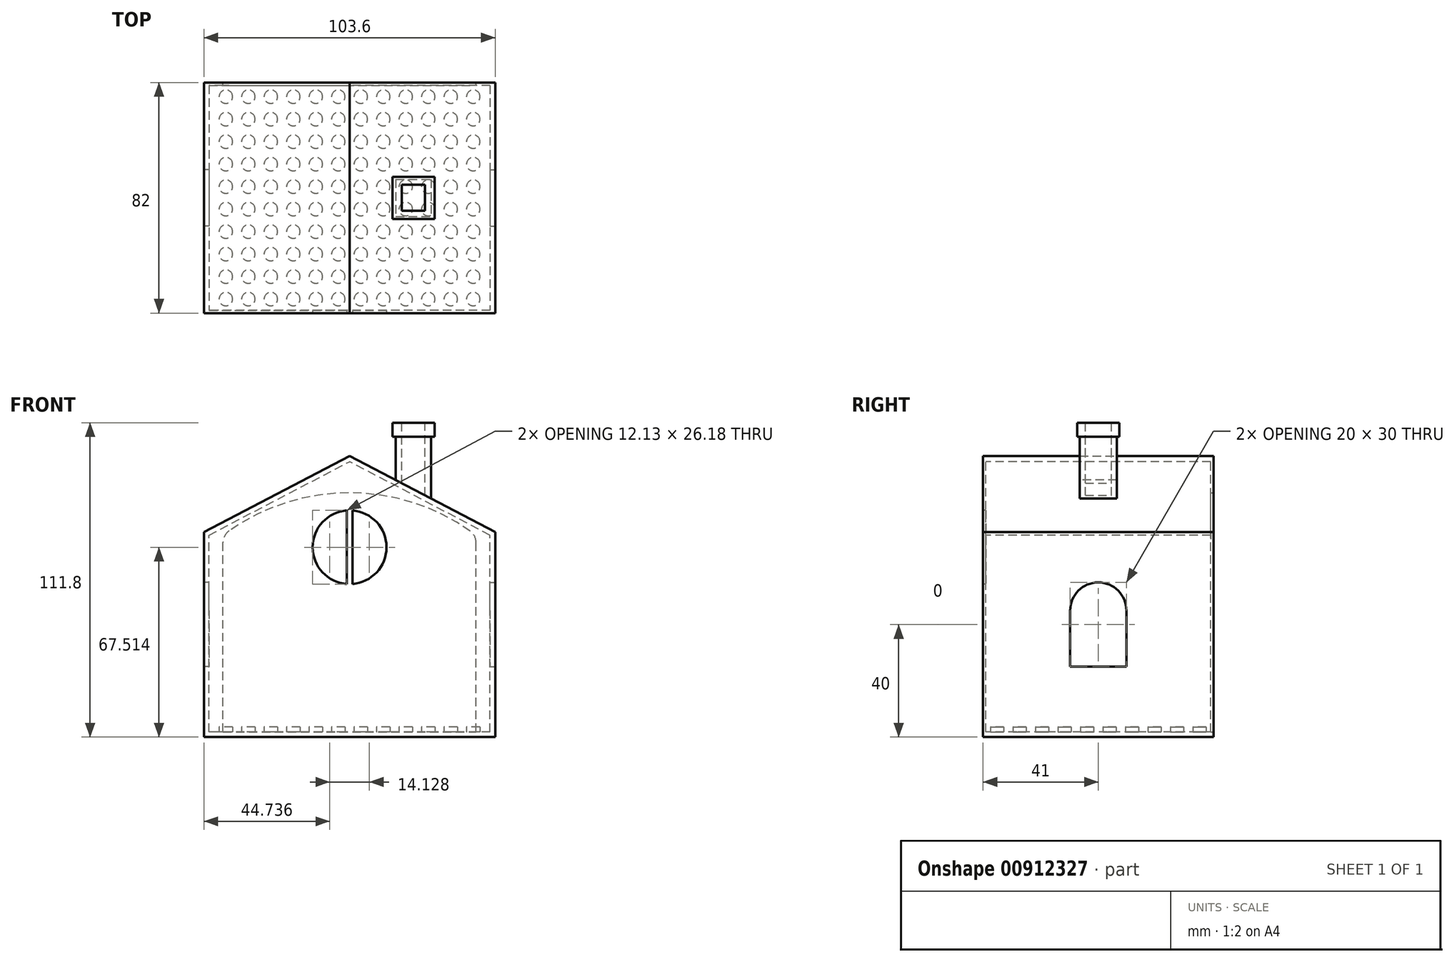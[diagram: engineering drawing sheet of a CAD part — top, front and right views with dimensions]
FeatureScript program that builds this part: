
annotation { "Feature Type Name" : "Feature", "Feature Type Description" : "" }
export const myFeature = defineFeature(function(context is Context, id is Id, definition is map)
    precondition{}
    {
        {
            var Q0;
            Q0=qCreatedBy(makeId("Front.planeOp"),FACE);
            var sketch = newSketch(context, id + "F0", { "sketchPlane" : qUnion([Q0])});
            skLineSegment(sketch, "E0", {"start": v(0, 0) * mm, "end": v(50, 0) * mm});
            skLineSegment(sketch, "E1", {"start": v(50, 0) * mm, "end": v(50, 70) * mm});
            skLineSegment(sketch, "E2", {"start": v(50, 70) * mm, "end": v(0, 96.17) * mm});
            skLineSegment(sketch, "E3", {"start": v(0, 96.17) * mm, "end": v(0, 0) * mm, "construction": true});
            skLineSegment(sketch, "E4.MirrorCS", {"start": v(-50, 70) * mm, "end": v(0, 96.17) * mm});
            skLineSegment(sketch, "E5.MirrorCS", {"start": v(-50, 0) * mm, "end": v(-50, 70) * mm});
            skLineSegment(sketch, "E6.MirrorCS", {"start": v(0, 0) * mm, "end": v(-50, 0) * mm});
            skLineSegment(sketch, "E7.0", {"start": v(0, -1.8) * mm, "end": v(51.8, -1.8) * mm});
            skLineSegment(sketch, "E7.1", {"start": v(51.8, 71.09) * mm, "end": v(0, 98.2) * mm});
            skLineSegment(sketch, "E7.2", {"start": v(-51.8, 71.09) * mm, "end": v(0, 98.2) * mm});
            skLineSegment(sketch, "E7.3", {"start": v(51.8, -1.8) * mm, "end": v(51.8, 71.09) * mm});
            skLineSegment(sketch, "E7.4", {"start": v(-51.8, -1.8) * mm, "end": v(-51.8, 71.09) * mm});
            skLineSegment(sketch, "E7.5", {"start": v(0, -1.8) * mm, "end": v(-51.8, -1.8) * mm});
            skSolve(sketch);
        }
        {
            var Q0;
            Q0=makeQuery(id+"F0.imprint","IMPRINT",FACE,{"disambiguationData":[TD([[makeQuery(id+"F0.imprint","IMPRINT",EDGE,{"derivedFrom":sQuery(id+"F0.wireOp",EDGE,"E0")}),-1.0]])]});
            var Q1;
            Q1=makeQuery(id+"F0.imprint","IMPRINT",FACE,{"disambiguationData":[TD([[makeQuery(id+"F0.imprint","IMPRINT",EDGE,{"derivedFrom":sQuery(id+"F0.wireOp",EDGE,"E0")}),1.0]])]});
            extrude(context, id + "F1", {"entities" : qUnion([Q0, Q1]), "endBound" : BoundingType.SYMMETRIC, "depth" : 82 * mm, "offsetDistance" : 25 * mm});
        }
        {
            var Q0;
            Q0=makeQuery(id+"F1.opExtrude","SWEPT_FACE",FACE,{"disambiguationData":[OSD([sQuery(id+"F0.wireOp",EDGE,"E7.4")])]});
            var sketch = newSketch(context, id + "F2", { "sketchPlane" : qUnion([Q0])});
            skLineSegment(sketch, "E8.top", {"start": v(-10, 23.2) * mm, "end": v(10, 23.2) * mm});
            skLineSegment(sketch, "E8.left", {"start": v(-10, 43.2) * mm, "end": v(-10, 23.2) * mm});
            skLineSegment(sketch, "E8.right", {"start": v(10, 43.2) * mm, "end": v(10, 23.2) * mm});
            skArc(sketch, "E9", {"start": v(10, 43.2) * mm, "mid": v(0, 53.2) * mm, "end": v(-10, 43.2) * mm});
            skSolve(sketch);
        }
        {
            var Q0;
            Q0=makeQuery(id+"F2.imprint","IMPRINT",FACE,{"disambiguationData":[TD([[makeQuery(id+"F2.imprint","IMPRINT",EDGE,{"derivedFrom":sQuery(id+"F2.wireOp",EDGE,"E8.bottom")}),-1.0]])]});
            var Q1;
            Q1=makeQuery(id+"F2.imprint","IMPRINT",FACE,{"disambiguationData":[TD([[makeQuery(id+"F2.imprint","IMPRINT",EDGE,{"derivedFrom":sQuery(id+"F2.wireOp",EDGE,"E8.top")}),1.0]])]});
            extrude(context, id + "F3", {"entities" : qUnion([Q0, Q1]), "operationType" : NewBodyOperationType.REMOVE, "oppositeDirection" : true, "depth" : 25 * mm, "offsetDistance" : 25 * mm});
        }
        {
            var Q0;
            Q0=makeQuery(id+"F1.opExtrude","SWEPT_FACE",FACE,{"disambiguationData":[OSD([sQuery(id+"F0.wireOp",EDGE,"E7.3")])]});
            var sketch = newSketch(context, id + "F4", { "sketchPlane" : qUnion([Q0])});
            skLineSegment(sketch, "E10.top", {"start": v(-10, 23.2) * mm, "end": v(10, 23.2) * mm});
            skLineSegment(sketch, "E10.left", {"start": v(-10, 43.2) * mm, "end": v(-10, 23.2) * mm});
            skLineSegment(sketch, "E10.right", {"start": v(10, 43.2) * mm, "end": v(10, 23.2) * mm});
            skArc(sketch, "E11", {"start": v(10, 43.2) * mm, "mid": v(0, 53.2) * mm, "end": v(-10, 43.2) * mm});
            skSolve(sketch);
        }
        {
            var Q0;
            Q0=makeQuery(id+"F4.imprint","IMPRINT",FACE,{"disambiguationData":[TD([[makeQuery(id+"F4.imprint","IMPRINT",EDGE,{"derivedFrom":sQuery(id+"F4.wireOp",EDGE,"E10.top")}),1.0]])]});
            extrude(context, id + "F5", {"entities" : qUnion([Q0]), "operationType" : NewBodyOperationType.REMOVE, "oppositeDirection" : true, "depth" : 25 * mm, "offsetDistance" : 25 * mm});
        }
        {
            var Q0;
            Q0=qCreatedBy(makeId("Front.planeOp"),FACE);
            cPlane(context, id + "F6", {"entities" : qUnion([Q0]), "cplaneType" : CPlaneType.OFFSET, "offset" : 40 * mm, "width" : 150 * mm, "height" : 150 * mm});
        }
        {
            var Q0;
            Q0=makeQuery(id+"F0.imprint","IMPRINT",FACE,{"disambiguationData":[TD([[makeQuery(id+"F0.imprint","IMPRINT",EDGE,{"derivedFrom":sQuery(id+"F0.wireOp",EDGE,"E0")}),1.0]])]});
            extrude(context, id + "F7", {"entities" : qUnion([Q0]), "operationType" : NewBodyOperationType.REMOVE, "oppositeDirection" : true, "depth" : 40 * mm, "offsetDistance" : 25 * mm});
        }
        {
            var Q0;
            Q0=makeQuery(id+"F0.imprint","IMPRINT",FACE,{"disambiguationData":[TD([[makeQuery(id+"F0.imprint","IMPRINT",EDGE,{"derivedFrom":sQuery(id+"F0.wireOp",EDGE,"E0")}),1.0]])]});
            extrude(context, id + "F8", {"entities" : qUnion([Q0]), "operationType" : NewBodyOperationType.REMOVE, "depth" : 40 * mm, "offsetDistance" : 25 * mm});
        }
        {
            var Q0;
            Q0=makeQuery(id+"F1.opExtrude","CAP_FACE",FACE,{"disambiguationData":[OSD([sQuery(id+"F0.wireOp",EDGE,"E7.0"),sQuery(id+"F0.wireOp",EDGE,"E7.1"),sQuery(id+"F0.wireOp",EDGE,"E7.2"),sQuery(id+"F0.wireOp",EDGE,"E7.3"),sQuery(id+"F0.wireOp",EDGE,"E7.4"),sQuery(id+"F0.wireOp",EDGE,"E7.5")])],"isStart":false});
            var sketch = newSketch(context, id + "F9", { "sketchPlane" : qUnion([Q0])});
            skCircle(sketch, "E12", {"center": v(0, 65.71) * mm, "radius": 13.13 * mm});
            skLineSegment(sketch, "E13", {"start": v(-13.13, 65.96) * mm, "end": v(13.13, 65.96) * mm, "construction": true});
            skLineSegment(sketch, "E14", {"start": v(0, 78.84) * mm, "end": v(0, 52.59) * mm, "construction": true});
            skLineSegment(sketch, "E15.0", {"start": v(-1, 78.84) * mm, "end": v(-1, 52.59) * mm});
            skLineSegment(sketch, "E16.0", {"start": v(1, 78.84) * mm, "end": v(1, 52.59) * mm});
            skSolve(sketch);
        }
        {
            var Q0;
            Q0=qCreatedBy(makeId("Top.planeOp"),FACE);
            var sketch = newSketch(context, id + "F10", { "sketchPlane" : qUnion([Q0])});
            skCircle(sketch, "E17", {"center": v(-44, 36) * mm, "radius": 2.4 * mm});
            skCircle(sketch, "E18.0.1.0", {"center": v(-44, 28) * mm, "radius": 2.4 * mm});
            skCircle(sketch, "E18.0.2.0", {"center": v(-44, 20) * mm, "radius": 2.4 * mm});
            skCircle(sketch, "E18.0.3.0", {"center": v(-44, 12) * mm, "radius": 2.4 * mm});
            skCircle(sketch, "E18.0.4.0", {"center": v(-44, 4) * mm, "radius": 2.4 * mm});
            skCircle(sketch, "E18.0.5.0", {"center": v(-44, -4) * mm, "radius": 2.4 * mm});
            skCircle(sketch, "E18.0.6.0", {"center": v(-44, -12) * mm, "radius": 2.4 * mm});
            skCircle(sketch, "E18.0.7.0", {"center": v(-44, -20) * mm, "radius": 2.4 * mm});
            skCircle(sketch, "E18.0.8.0", {"center": v(-44, -28) * mm, "radius": 2.4 * mm});
            skCircle(sketch, "E18.0.9.0", {"center": v(-44, -36) * mm, "radius": 2.4 * mm});
            skCircle(sketch, "E18.1.0.0", {"center": v(-36, 36) * mm, "radius": 2.4 * mm});
            skCircle(sketch, "E18.1.1.0", {"center": v(-36, 28) * mm, "radius": 2.4 * mm});
            skCircle(sketch, "E18.1.2.0", {"center": v(-36, 20) * mm, "radius": 2.4 * mm});
            skCircle(sketch, "E18.1.3.0", {"center": v(-36, 12) * mm, "radius": 2.4 * mm});
            skCircle(sketch, "E18.1.4.0", {"center": v(-36, 4) * mm, "radius": 2.4 * mm});
            skCircle(sketch, "E18.1.5.0", {"center": v(-36, -4) * mm, "radius": 2.4 * mm});
            skCircle(sketch, "E18.1.6.0", {"center": v(-36, -12) * mm, "radius": 2.4 * mm});
            skCircle(sketch, "E18.1.7.0", {"center": v(-36, -20) * mm, "radius": 2.4 * mm});
            skCircle(sketch, "E18.1.8.0", {"center": v(-36, -28) * mm, "radius": 2.4 * mm});
            skCircle(sketch, "E18.1.9.0", {"center": v(-36, -36) * mm, "radius": 2.4 * mm});
            skCircle(sketch, "E18.2.0.0", {"center": v(-28, 36) * mm, "radius": 2.4 * mm});
            skCircle(sketch, "E18.2.1.0", {"center": v(-28, 28) * mm, "radius": 2.4 * mm});
            skCircle(sketch, "E18.2.2.0", {"center": v(-28, 20) * mm, "radius": 2.4 * mm});
            skCircle(sketch, "E18.2.3.0", {"center": v(-28, 12) * mm, "radius": 2.4 * mm});
            skCircle(sketch, "E18.2.4.0", {"center": v(-28, 4) * mm, "radius": 2.4 * mm});
            skCircle(sketch, "E18.2.5.0", {"center": v(-28, -4) * mm, "radius": 2.4 * mm});
            skCircle(sketch, "E18.2.6.0", {"center": v(-28, -12) * mm, "radius": 2.4 * mm});
            skCircle(sketch, "E18.2.7.0", {"center": v(-28, -20) * mm, "radius": 2.4 * mm});
            skCircle(sketch, "E18.2.8.0", {"center": v(-28, -28) * mm, "radius": 2.4 * mm});
            skCircle(sketch, "E18.2.9.0", {"center": v(-28, -36) * mm, "radius": 2.4 * mm});
            skCircle(sketch, "E18.3.0.0", {"center": v(-20, 36) * mm, "radius": 2.4 * mm});
            skCircle(sketch, "E18.3.1.0", {"center": v(-20, 28) * mm, "radius": 2.4 * mm});
            skCircle(sketch, "E18.3.2.0", {"center": v(-20, 20) * mm, "radius": 2.4 * mm});
            skCircle(sketch, "E18.3.3.0", {"center": v(-20, 12) * mm, "radius": 2.4 * mm});
            skCircle(sketch, "E18.3.4.0", {"center": v(-20, 4) * mm, "radius": 2.4 * mm});
            skCircle(sketch, "E18.3.5.0", {"center": v(-20, -4) * mm, "radius": 2.4 * mm});
            skCircle(sketch, "E18.3.6.0", {"center": v(-20, -12) * mm, "radius": 2.4 * mm});
            skCircle(sketch, "E18.3.7.0", {"center": v(-20, -20) * mm, "radius": 2.4 * mm});
            skCircle(sketch, "E18.3.8.0", {"center": v(-20, -28) * mm, "radius": 2.4 * mm});
            skCircle(sketch, "E18.3.9.0", {"center": v(-20, -36) * mm, "radius": 2.4 * mm});
            skCircle(sketch, "E18.4.0.0", {"center": v(-12, 36) * mm, "radius": 2.4 * mm});
            skCircle(sketch, "E18.4.1.0", {"center": v(-12, 28) * mm, "radius": 2.4 * mm});
            skCircle(sketch, "E18.4.2.0", {"center": v(-12, 20) * mm, "radius": 2.4 * mm});
            skCircle(sketch, "E18.4.3.0", {"center": v(-12, 12) * mm, "radius": 2.4 * mm});
            skCircle(sketch, "E18.4.4.0", {"center": v(-12, 4) * mm, "radius": 2.4 * mm});
            skCircle(sketch, "E18.4.5.0", {"center": v(-12, -4) * mm, "radius": 2.4 * mm});
            skCircle(sketch, "E18.4.6.0", {"center": v(-12, -12) * mm, "radius": 2.4 * mm});
            skCircle(sketch, "E18.4.7.0", {"center": v(-12, -20) * mm, "radius": 2.4 * mm});
            skCircle(sketch, "E18.4.8.0", {"center": v(-12, -28) * mm, "radius": 2.4 * mm});
            skCircle(sketch, "E18.4.9.0", {"center": v(-12, -36) * mm, "radius": 2.4 * mm});
            skCircle(sketch, "E18.5.0.0", {"center": v(-4, 36) * mm, "radius": 2.4 * mm});
            skCircle(sketch, "E18.5.1.0", {"center": v(-4, 28) * mm, "radius": 2.4 * mm});
            skCircle(sketch, "E18.5.2.0", {"center": v(-4, 20) * mm, "radius": 2.4 * mm});
            skCircle(sketch, "E18.5.3.0", {"center": v(-4, 12) * mm, "radius": 2.4 * mm});
            skCircle(sketch, "E18.5.4.0", {"center": v(-4, 4) * mm, "radius": 2.4 * mm});
            skCircle(sketch, "E18.5.5.0", {"center": v(-4, -4) * mm, "radius": 2.4 * mm});
            skCircle(sketch, "E18.5.6.0", {"center": v(-4, -12) * mm, "radius": 2.4 * mm});
            skCircle(sketch, "E18.5.7.0", {"center": v(-4, -20) * mm, "radius": 2.4 * mm});
            skCircle(sketch, "E18.5.8.0", {"center": v(-4, -28) * mm, "radius": 2.4 * mm});
            skCircle(sketch, "E18.5.9.0", {"center": v(-4, -36) * mm, "radius": 2.4 * mm});
            skCircle(sketch, "E18.6.0.0", {"center": v(4, 36) * mm, "radius": 2.4 * mm});
            skCircle(sketch, "E18.6.1.0", {"center": v(4, 28) * mm, "radius": 2.4 * mm});
            skCircle(sketch, "E18.6.2.0", {"center": v(4, 20) * mm, "radius": 2.4 * mm});
            skCircle(sketch, "E18.6.3.0", {"center": v(4, 12) * mm, "radius": 2.4 * mm});
            skCircle(sketch, "E18.6.4.0", {"center": v(4, 4) * mm, "radius": 2.4 * mm});
            skCircle(sketch, "E18.6.5.0", {"center": v(4, -4) * mm, "radius": 2.4 * mm});
            skCircle(sketch, "E18.6.6.0", {"center": v(4, -12) * mm, "radius": 2.4 * mm});
            skCircle(sketch, "E18.6.7.0", {"center": v(4, -20) * mm, "radius": 2.4 * mm});
            skCircle(sketch, "E18.6.8.0", {"center": v(4, -28) * mm, "radius": 2.4 * mm});
            skCircle(sketch, "E18.6.9.0", {"center": v(4, -36) * mm, "radius": 2.4 * mm});
            skCircle(sketch, "E18.7.0.0", {"center": v(12, 36) * mm, "radius": 2.4 * mm});
            skCircle(sketch, "E18.7.1.0", {"center": v(12, 28) * mm, "radius": 2.4 * mm});
            skCircle(sketch, "E18.7.2.0", {"center": v(12, 20) * mm, "radius": 2.4 * mm});
            skCircle(sketch, "E18.7.3.0", {"center": v(12, 12) * mm, "radius": 2.4 * mm});
            skCircle(sketch, "E18.7.4.0", {"center": v(12, 4) * mm, "radius": 2.4 * mm});
            skCircle(sketch, "E18.7.5.0", {"center": v(12, -4) * mm, "radius": 2.4 * mm});
            skCircle(sketch, "E18.7.6.0", {"center": v(12, -12) * mm, "radius": 2.4 * mm});
            skCircle(sketch, "E18.7.7.0", {"center": v(12, -20) * mm, "radius": 2.4 * mm});
            skCircle(sketch, "E18.7.8.0", {"center": v(12, -28) * mm, "radius": 2.4 * mm});
            skCircle(sketch, "E18.7.9.0", {"center": v(12, -36) * mm, "radius": 2.4 * mm});
            skCircle(sketch, "E18.8.0.0", {"center": v(20, 36) * mm, "radius": 2.4 * mm});
            skCircle(sketch, "E18.8.1.0", {"center": v(20, 28) * mm, "radius": 2.4 * mm});
            skCircle(sketch, "E18.8.2.0", {"center": v(20, 20) * mm, "radius": 2.4 * mm});
            skCircle(sketch, "E18.8.3.0", {"center": v(20, 12) * mm, "radius": 2.4 * mm});
            skCircle(sketch, "E18.8.4.0", {"center": v(20, 4) * mm, "radius": 2.4 * mm});
            skCircle(sketch, "E18.8.5.0", {"center": v(20, -4) * mm, "radius": 2.4 * mm});
            skCircle(sketch, "E18.8.6.0", {"center": v(20, -12) * mm, "radius": 2.4 * mm});
            skCircle(sketch, "E18.8.7.0", {"center": v(20, -20) * mm, "radius": 2.4 * mm});
            skCircle(sketch, "E18.8.8.0", {"center": v(20, -28) * mm, "radius": 2.4 * mm});
            skCircle(sketch, "E18.8.9.0", {"center": v(20, -36) * mm, "radius": 2.4 * mm});
            skCircle(sketch, "E18.9.0.0", {"center": v(28, 36) * mm, "radius": 2.4 * mm});
            skCircle(sketch, "E18.9.1.0", {"center": v(28, 28) * mm, "radius": 2.4 * mm});
            skCircle(sketch, "E18.9.2.0", {"center": v(28, 20) * mm, "radius": 2.4 * mm});
            skCircle(sketch, "E18.9.3.0", {"center": v(28, 12) * mm, "radius": 2.4 * mm});
            skCircle(sketch, "E18.9.4.0", {"center": v(28, 4) * mm, "radius": 2.4 * mm});
            skCircle(sketch, "E18.9.5.0", {"center": v(28, -4) * mm, "radius": 2.4 * mm});
            skCircle(sketch, "E18.9.6.0", {"center": v(28, -12) * mm, "radius": 2.4 * mm});
            skCircle(sketch, "E18.9.7.0", {"center": v(28, -20) * mm, "radius": 2.4 * mm});
            skCircle(sketch, "E18.9.8.0", {"center": v(28, -28) * mm, "radius": 2.4 * mm});
            skCircle(sketch, "E18.9.9.0", {"center": v(28, -36) * mm, "radius": 2.4 * mm});
            skCircle(sketch, "E18.10.0.0", {"center": v(36, 36) * mm, "radius": 2.4 * mm});
            skCircle(sketch, "E18.10.1.0", {"center": v(36, 28) * mm, "radius": 2.4 * mm});
            skCircle(sketch, "E18.10.2.0", {"center": v(36, 20) * mm, "radius": 2.4 * mm});
            skCircle(sketch, "E18.10.3.0", {"center": v(36, 12) * mm, "radius": 2.4 * mm});
            skCircle(sketch, "E18.10.4.0", {"center": v(36, 4) * mm, "radius": 2.4 * mm});
            skCircle(sketch, "E18.10.5.0", {"center": v(36, -4) * mm, "radius": 2.4 * mm});
            skCircle(sketch, "E18.10.6.0", {"center": v(36, -12) * mm, "radius": 2.4 * mm});
            skCircle(sketch, "E18.10.7.0", {"center": v(36, -20) * mm, "radius": 2.4 * mm});
            skCircle(sketch, "E18.10.8.0", {"center": v(36, -28) * mm, "radius": 2.4 * mm});
            skCircle(sketch, "E18.10.9.0", {"center": v(36, -36) * mm, "radius": 2.4 * mm});
            skCircle(sketch, "E18.11.0.0", {"center": v(44, 36) * mm, "radius": 2.4 * mm});
            skCircle(sketch, "E18.11.1.0", {"center": v(44, 28) * mm, "radius": 2.4 * mm});
            skCircle(sketch, "E18.11.2.0", {"center": v(44, 20) * mm, "radius": 2.4 * mm});
            skCircle(sketch, "E18.11.3.0", {"center": v(44, 12) * mm, "radius": 2.4 * mm});
            skCircle(sketch, "E18.11.4.0", {"center": v(44, 4) * mm, "radius": 2.4 * mm});
            skCircle(sketch, "E18.11.5.0", {"center": v(44, -4) * mm, "radius": 2.4 * mm});
            skCircle(sketch, "E18.11.6.0", {"center": v(44, -12) * mm, "radius": 2.4 * mm});
            skCircle(sketch, "E18.11.7.0", {"center": v(44, -20) * mm, "radius": 2.4 * mm});
            skCircle(sketch, "E18.11.8.0", {"center": v(44, -28) * mm, "radius": 2.4 * mm});
            skCircle(sketch, "E18.11.9.0", {"center": v(44, -36) * mm, "radius": 2.4 * mm});
            skLineSegment(sketch, "E18.direction1", {"start": v(-44, 36) * mm, "end": v(-36, 36) * mm, "construction": true});
            skLineSegment(sketch, "E18.direction2", {"start": v(-44, 36) * mm, "end": v(-44, 28) * mm, "construction": true});
            skSolve(sketch);
        }
        {
            var Q0;
            Q0=qSketchRegion(id+"F10",true);
            extrude(context, id + "F11", {"entities" : qUnion([Q0]), "operationType" : NewBodyOperationType.ADD, "depth" : 1.8 * mm, "offsetDistance" : 25 * mm});
        }
        {
            var Q0;
            {var subQ0=sQuery(id+"F9.wireOp",EDGE,"E15.0");var subQ1=sQuery(id+"F9.wireOp",EDGE,"E12");var subQ2=makeQuery(id+"F9.imprint","INTERSECT",VERTEX,{"disambiguationData":[OD(0.0)],"derivedFrom":[subQ1,subQ0]});Q0=makeQuery(id+"F9.imprint","IMPRINT",FACE,{"disambiguationData":[TD([[makeQuery(id+"F9.imprint","IMPRINT",EDGE,{"disambiguationData":[TD([[subQ2,-1.0]])],"derivedFrom":subQ1}),1.0]])]});}
            var Q1;
            {var subQ0=sQuery(id+"F9.wireOp",EDGE,"E16.0");var subQ1=sQuery(id+"F9.wireOp",EDGE,"E12");var subQ2=makeQuery(id+"F9.imprint","INTERSECT",VERTEX,{"disambiguationData":[OD(0.0)],"derivedFrom":[subQ1,subQ0]});Q1=makeQuery(id+"F9.imprint","IMPRINT",FACE,{"disambiguationData":[TD([[makeQuery(id+"F9.imprint","IMPRINT",EDGE,{"disambiguationData":[TD([[subQ2,1.0]])],"derivedFrom":subQ1}),1.0]])]});}
            extrude(context, id + "F12", {"entities" : qUnion([Q0, Q1]), "operationType" : NewBodyOperationType.REMOVE, "oppositeDirection" : true, "depth" : 25 * mm, "offsetDistance" : 25 * mm});
        }
        {
            var Q0;
            Q0=qCreatedBy(makeId("Top.planeOp"),FACE);
            cPlane(context, id + "F13", {"entities" : qUnion([Q0]), "cplaneType" : CPlaneType.OFFSET, "offset" : 110 * mm, "width" : 150 * mm, "height" : 150 * mm});
        }
        {
            var Q0;
            Q0=qCreatedBy(id+"F13.planeOp",FACE);
            var sketch = newSketch(context, id + "F14", { "sketchPlane" : qUnion([Q0])});
            skLineSegment(sketch, "E19.bottom", {"start": v(16.41, 6.6) * mm, "end": v(29.03, 6.6) * mm});
            skLineSegment(sketch, "E19.top", {"start": v(16.41, -6.6) * mm, "end": v(29.03, -6.6) * mm});
            skLineSegment(sketch, "E19.left", {"start": v(16.41, 6.6) * mm, "end": v(16.41, -6.6) * mm});
            skLineSegment(sketch, "E19.right", {"start": v(29.03, 6.6) * mm, "end": v(29.03, -6.6) * mm});
            skLineSegment(sketch, "E20", {"start": v(16.41, 0) * mm, "end": v(29.03, 0) * mm, "construction": true});
            skLineSegment(sketch, "E21", {"start": v(22.72, 6.6) * mm, "end": v(22.72, -6.6) * mm, "construction": true});
            skLineSegment(sketch, "E22.bottom", {"start": v(26.86, -4.63) * mm, "end": v(18.58, -4.63) * mm});
            skLineSegment(sketch, "E22.top", {"start": v(26.86, 4.63) * mm, "end": v(18.58, 4.63) * mm});
            skLineSegment(sketch, "E22.left", {"start": v(26.86, -4.63) * mm, "end": v(26.86, 4.63) * mm});
            skLineSegment(sketch, "E22.right", {"start": v(18.58, -4.63) * mm, "end": v(18.58, 4.63) * mm});
            skPoint(sketch, "E22.middle", {"position": v(22.72, 0) * mm});
            skLineSegment(sketch, "E23.bottom", {"start": v(30.22, -7.5) * mm, "end": v(15.21, -7.5) * mm});
            skLineSegment(sketch, "E23.top", {"start": v(30.22, 7.5) * mm, "end": v(15.21, 7.5) * mm});
            skLineSegment(sketch, "E23.left", {"start": v(30.22, -7.5) * mm, "end": v(30.22, 7.5) * mm});
            skLineSegment(sketch, "E23.right", {"start": v(15.21, -7.5) * mm, "end": v(15.21, 7.5) * mm});
            skSolve(sketch);
        }
        {
            var Q0;
            Q0=makeQuery(id+"F14.imprint","IMPRINT",FACE,{"disambiguationData":[TD([[makeQuery(id+"F14.imprint","IMPRINT",EDGE,{"derivedFrom":sQuery(id+"F14.wireOp",EDGE,"E19.bottom")}),-1.0]])]});
            extrude(context, id + "F15", {"entities" : qUnion([Q0]), "operationType" : NewBodyOperationType.ADD, "endBound" : BoundingType.UP_TO_NEXT, "oppositeDirection" : true, "depth" : 25 * mm, "offsetDistance" : 25 * mm});
        }
        {
            var Q0;
            Q0=makeQuery(id+"F14.imprint","IMPRINT",FACE,{"disambiguationData":[TD([[makeQuery(id+"F14.imprint","IMPRINT",EDGE,{"derivedFrom":sQuery(id+"F14.wireOp",EDGE,"E19.bottom")}),1.0]])]});
            extrude(context, id + "F16", {"entities" : qUnion([Q0]), "operationType" : NewBodyOperationType.ADD, "oppositeDirection" : true, "depth" : 5 * mm, "offsetDistance" : 25 * mm});
        }
        {
            var Q0;
            Q0=makeQuery(id+"F1.opExtrude","CAP_FACE",FACE,{"disambiguationData":[OSD([sQuery(id+"F0.wireOp",EDGE,"E7.0"),sQuery(id+"F0.wireOp",EDGE,"E7.1"),sQuery(id+"F0.wireOp",EDGE,"E7.2"),sQuery(id+"F0.wireOp",EDGE,"E7.3"),sQuery(id+"F0.wireOp",EDGE,"E7.4"),sQuery(id+"F0.wireOp",EDGE,"E7.5")])],"isStart":true});
            var sketch = newSketch(context, id + "F17", { "sketchPlane" : qUnion([Q0])});
            skLineSegment(sketch, "E24", {"start": v(45, 0) * mm, "end": v(-45, 0) * mm});
            skLineSegment(sketch, "E25", {"start": v(-45, 0) * mm, "end": v(-45, 70) * mm});
            skLineSegment(sketch, "E26", {"start": v(45, 0) * mm, "end": v(45, 70) * mm});
            skLineSegment(sketch, "E27", {"start": v(-45, 70) * mm, "end": v(45, 70) * mm, "construction": true});
            skArc(sketch, "E28", {"start": v(45, 70) * mm, "mid": v(0, 85.09) * mm, "end": v(-45, 70) * mm});
            skSolve(sketch);
        }
        {
            var Q0;
            Q0=makeQuery(id+"F17.imprint","IMPRINT",FACE,{"disambiguationData":[TD([[makeQuery(id+"F17.imprint","IMPRINT",EDGE,{"derivedFrom":sQuery(id+"F17.wireOp",EDGE,"E24")}),-1.0]])]});
            extrude(context, id + "F18", {"entities" : qUnion([Q0]), "operationType" : NewBodyOperationType.REMOVE, "oppositeDirection" : true, "depth" : 1 * mm, "offsetDistance" : 25 * mm});
        }
        {
            var Q0;
            Q0=makeQuery(id+"F18.boolean.opBoolean","COPY",EDGE,{"derivedFrom":makeQuery(id+"F18.opExtrude","SWEPT_EDGE",EDGE,{"disambiguationData":[OSD([sQuery(id+"F17.wireOp",EDGE,"E25"),sQuery(id+"F17.wireOp",EDGE,"E28")])]})});
            var Q1;
            Q1=makeQuery(id+"F18.boolean.opBoolean","COPY",EDGE,{"derivedFrom":makeQuery(id+"F18.opExtrude","SWEPT_EDGE",EDGE,{"disambiguationData":[OSD([sQuery(id+"F17.wireOp",EDGE,"E26"),sQuery(id+"F17.wireOp",EDGE,"E28")])]})});
            fillet(context, id + "F19", {"entities" : qUnion([Q0, Q1]), "radius" : 5 * mm, "tangentPropagation" : true, "allowEdgeOverflow" : false});
        }
    });
